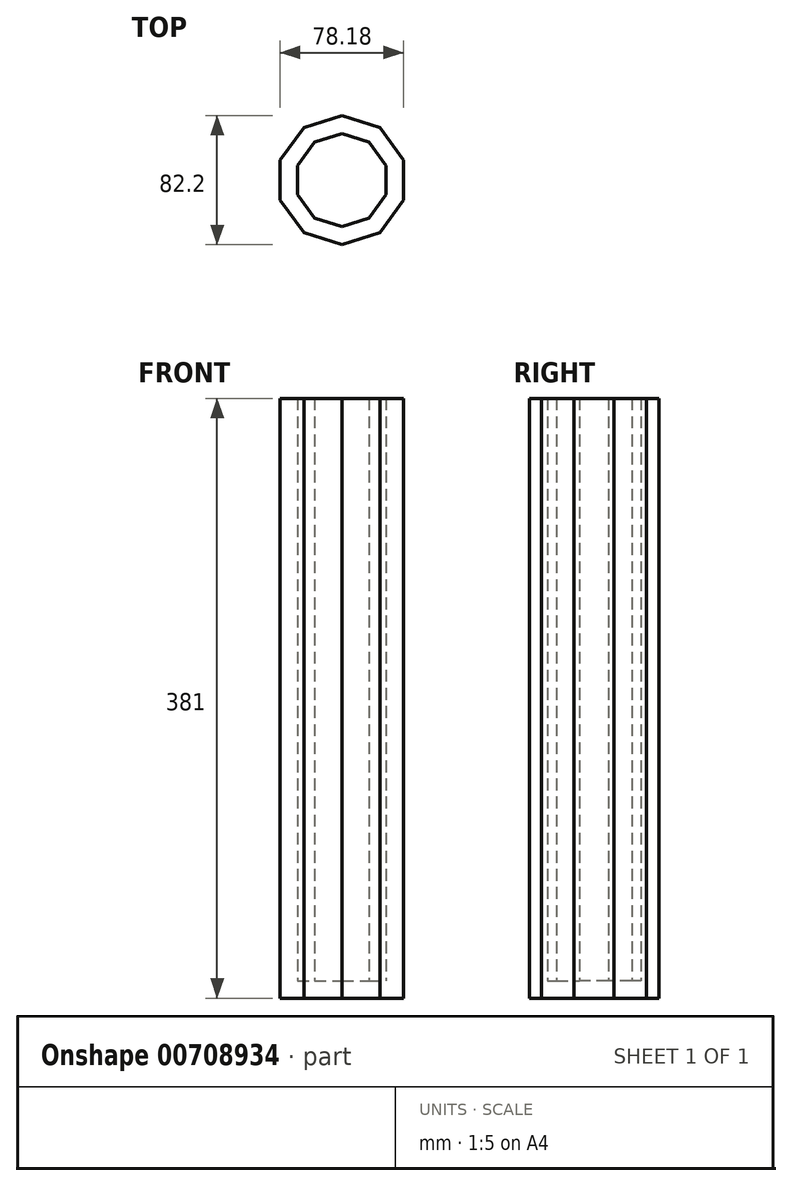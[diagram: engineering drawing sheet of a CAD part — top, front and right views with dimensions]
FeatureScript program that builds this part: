
annotation { "Feature Type Name" : "Feature", "Feature Type Description" : "" }
export const myFeature = defineFeature(function(context is Context, id is Id, definition is map)
    precondition{}
    {
        {
            var Q0;
            Q0=qCreatedBy(makeId("Top.planeOp"),FACE);
            var sketch = newSketch(context, id + "F0", { "sketchPlane" : qUnion([Q0])});
            skCircle(sketch, "E0.cCircle", {"center": v(0, 0) * mm, "radius": 39.09 * mm, "construction": true});
            skLineSegment(sketch, "E0.0", {"start": v(39.09, 12.7) * mm, "end": v(39.09, -12.7) * mm});
            skLineSegment(sketch, "E0.1", {"start": v(39.09, -12.7) * mm, "end": v(24.16, -33.25) * mm});
            skLineSegment(sketch, "E0.2", {"start": v(24.16, -33.25) * mm, "end": v(0, -41.1) * mm});
            skLineSegment(sketch, "E0.3", {"start": v(0, -41.1) * mm, "end": v(-24.16, -33.25) * mm});
            skLineSegment(sketch, "E0.4", {"start": v(-24.16, -33.25) * mm, "end": v(-39.09, -12.7) * mm});
            skLineSegment(sketch, "E0.5", {"start": v(-39.09, -12.7) * mm, "end": v(-39.09, 12.7) * mm});
            skLineSegment(sketch, "E0.6", {"start": v(-39.09, 12.7) * mm, "end": v(-24.16, 33.25) * mm});
            skLineSegment(sketch, "E0.7", {"start": v(-24.16, 33.25) * mm, "end": v(0, 41.1) * mm});
            skLineSegment(sketch, "E0.8", {"start": v(0, 41.1) * mm, "end": v(24.16, 33.25) * mm});
            skLineSegment(sketch, "E0.9", {"start": v(24.16, 33.25) * mm, "end": v(39.09, 12.7) * mm});
            skPoint(sketch, "E0.0.midPoint", {"position": v(39.09, 0) * mm});
            skSolve(sketch);
        }
        {
            var Q0;
            Q0=makeQuery(id+"F0.imprint","IMPRINT",FACE,{"disambiguationData":[TD([[makeQuery(id+"F0.imprint","IMPRINT",EDGE,{"derivedFrom":sQuery(id+"F0.wireOp",EDGE,"E0.0")}),-1.0]])]});
            extrude(context, id + "F1", {"entities" : qUnion([Q0]), "depth" : 381 * mm, "offsetDistance" : 25.4 * mm});
        }
        {
            var Q0;
            Q0=makeQuery(id+"F1.opExtrude","CAP_FACE",FACE,{"disambiguationData":[OSD([sQuery(id+"F0.wireOp",EDGE,"E0.0"),sQuery(id+"F0.wireOp",EDGE,"E0.1"),sQuery(id+"F0.wireOp",EDGE,"E0.2"),sQuery(id+"F0.wireOp",EDGE,"E0.3"),sQuery(id+"F0.wireOp",EDGE,"E0.4"),sQuery(id+"F0.wireOp",EDGE,"E0.5"),sQuery(id+"F0.wireOp",EDGE,"E0.6"),sQuery(id+"F0.wireOp",EDGE,"E0.7"),sQuery(id+"F0.wireOp",EDGE,"E0.8"),sQuery(id+"F0.wireOp",EDGE,"E0.9")])],"isStart":false});
            shell(context, id + "F2", {"entities" : qUnion([Q0]), "thickness" : 10.9 * mm});
        }
    });
